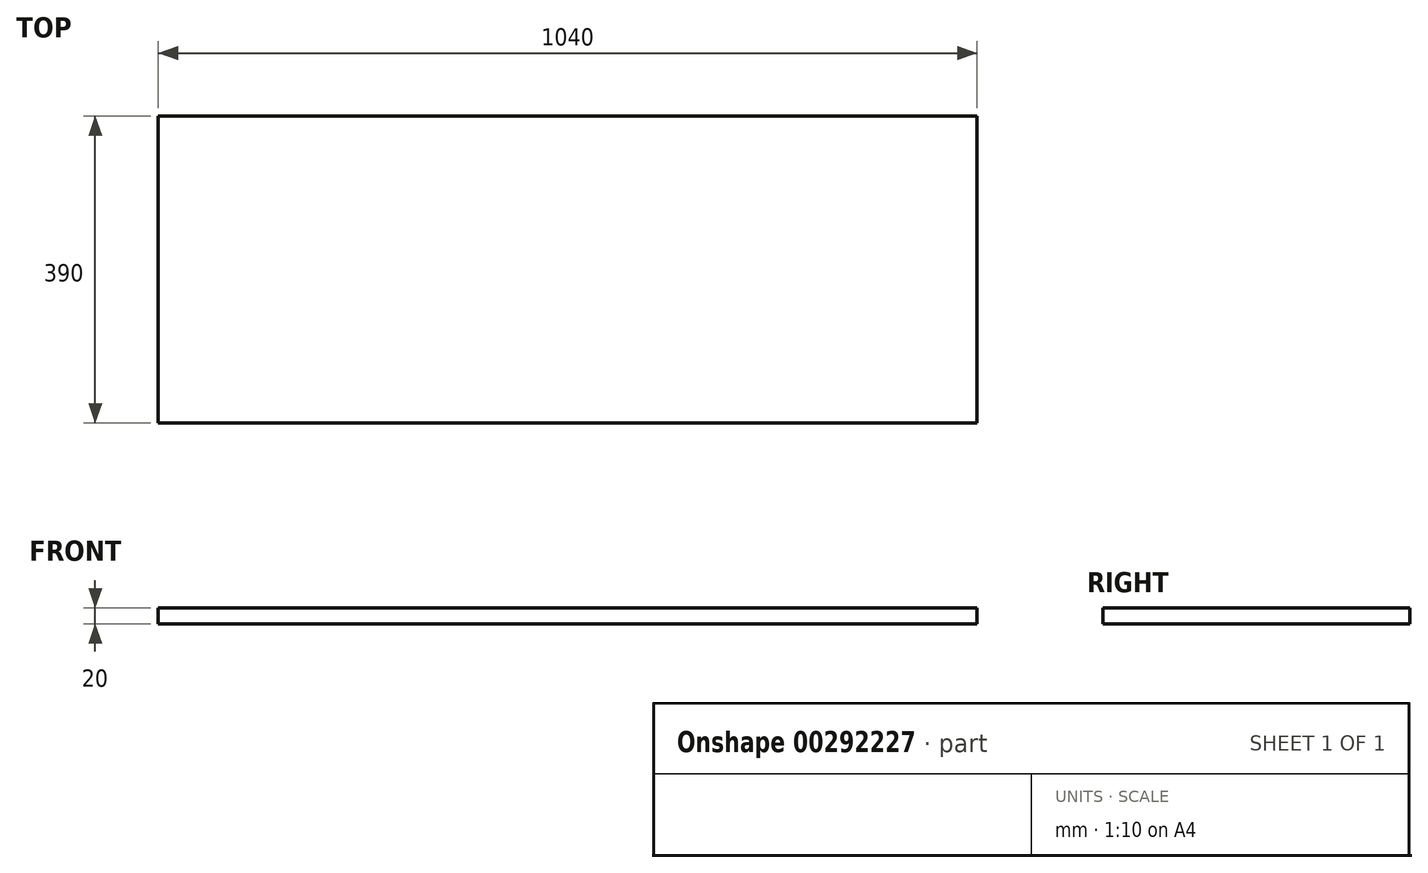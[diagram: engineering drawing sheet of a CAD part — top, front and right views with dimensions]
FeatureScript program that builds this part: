
annotation { "Feature Type Name" : "Feature", "Feature Type Description" : "" }
export const myFeature = defineFeature(function(context is Context, id is Id, definition is map)
    precondition{}
    {
        {
            var Q0;
            Q0=qCreatedBy(makeId("Top.planeOp"),FACE);
            var sketch = newSketch(context, id + "F0", { "sketchPlane" : qUnion([Q0])});
            skLineSegment(sketch, "E0.bottom", {"start": v(520, -195) * mm, "end": v(-520, -195) * mm});
            skLineSegment(sketch, "E0.top", {"start": v(520, 195) * mm, "end": v(-520, 195) * mm});
            skLineSegment(sketch, "E0.left", {"start": v(520, -195) * mm, "end": v(520, 195) * mm});
            skLineSegment(sketch, "E0.right", {"start": v(-520, -195) * mm, "end": v(-520, 195) * mm});
            skPoint(sketch, "E0.middle", {"position": v(0, 0) * mm});
            skSolve(sketch);
        }
        {
            var Q0;
            Q0 = qSketchRegion(id + "F0", true);
            extrude(context, id + "F1", {"entities" : qUnion([Q0]), "depth" : 20 * mm});
        }
    });
